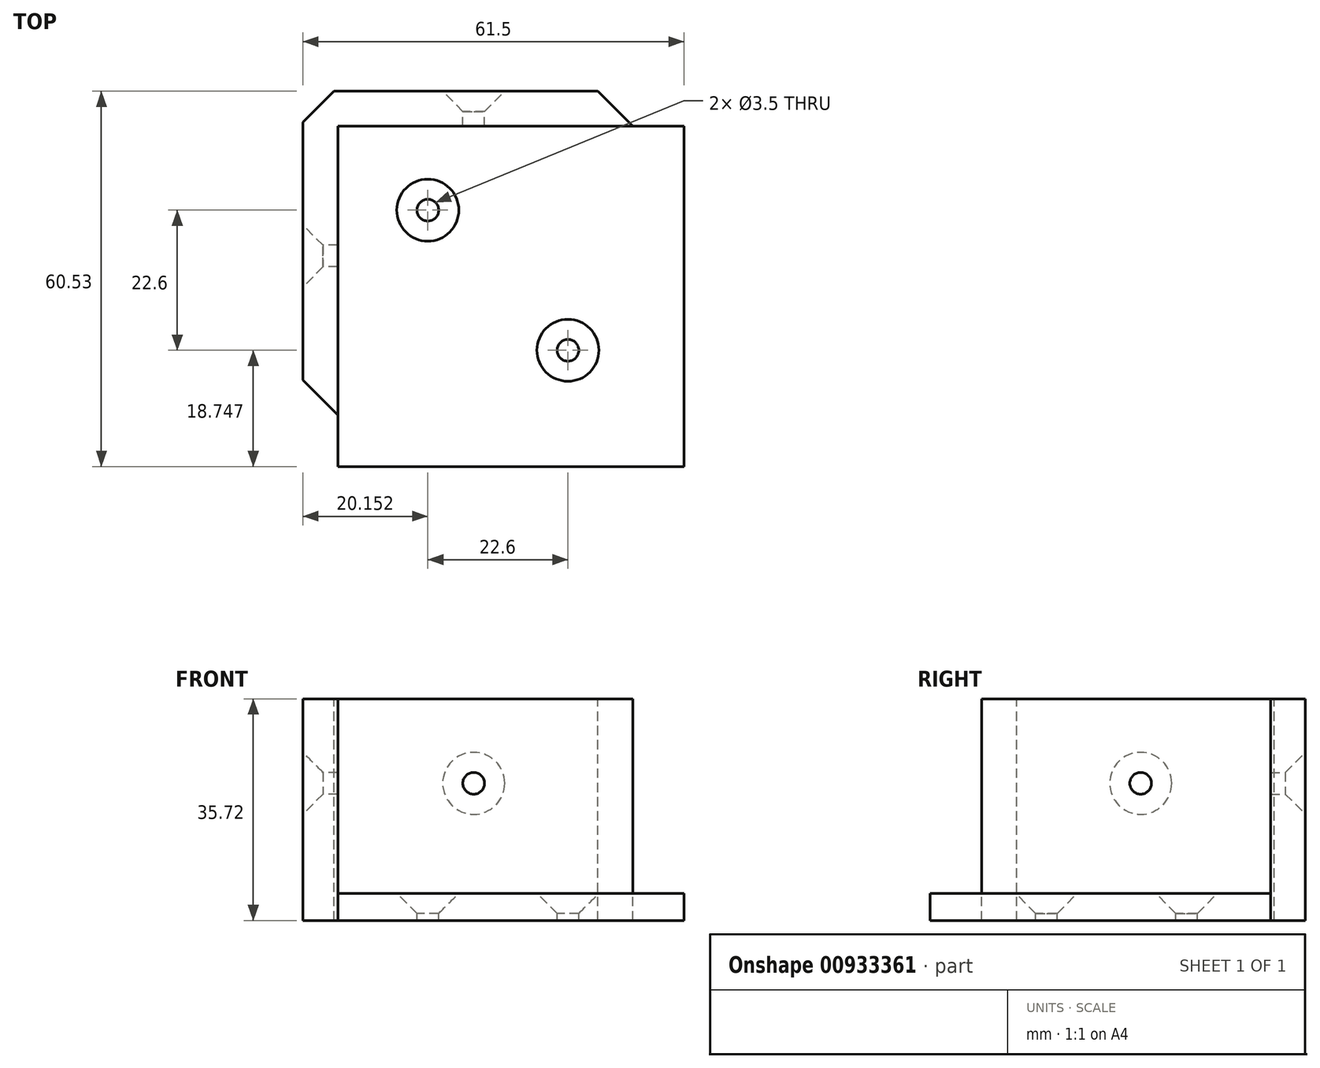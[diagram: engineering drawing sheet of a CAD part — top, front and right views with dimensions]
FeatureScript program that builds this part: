
annotation { "Feature Type Name" : "Feature", "Feature Type Description" : "" }
export const myFeature = defineFeature(function(context is Context, id is Id, definition is map)
    precondition{}
    {
        {
            var Q0;
            Q0=qCreatedBy(makeId("Top.planeOp"),FACE);
            var sketch = newSketch(context, id + "F0", { "sketchPlane" : qUnion([Q0])});
            skLineSegment(sketch, "E0.bottom", {"start": v(-41.05, 39.15) * mm, "end": v(20.45, 39.15) * mm});
            skLineSegment(sketch, "E0.top", {"start": v(-41.05, -21.38) * mm, "end": v(20.45, -21.38) * mm});
            skLineSegment(sketch, "E0.left", {"start": v(-41.05, 39.15) * mm, "end": v(-41.05, -21.38) * mm});
            skLineSegment(sketch, "E0.right", {"start": v(20.45, 39.15) * mm, "end": v(20.45, -21.38) * mm});
            skSolve(sketch);
        }
        {
            var Q0;
            Q0=makeQuery(id+"F0.imprint","IMPRINT",FACE,{"disambiguationData":[TD([[makeQuery(id+"F0.imprint","IMPRINT",EDGE,{"derivedFrom":sQuery(id+"F0.wireOp",EDGE,"E0.bottom")}),-1.0]])]});
            extrude(context, id + "F1", {"entities" : qUnion([Q0]), "depth" : 4.38 * mm, "offsetDistance" : 25 * mm});
        }
        {
            var Q0;
            Q0=makeQuery(id+"F1.opExtrude","CAP_FACE",FACE,{"disambiguationData":[OSD([sQuery(id+"F0.wireOp",EDGE,"E0.bottom"),sQuery(id+"F0.wireOp",EDGE,"E0.top"),sQuery(id+"F0.wireOp",EDGE,"E0.left"),sQuery(id+"F0.wireOp",EDGE,"E0.right")])],"isStart":false});
            var sketch = newSketch(context, id + "F2", { "sketchPlane" : qUnion([Q0])});
            skLineSegment(sketch, "E1.bottom", {"start": v(-41.05, -21.38) * mm, "end": v(-35.4, -21.38) * mm});
            skLineSegment(sketch, "E1.top", {"start": v(-41.05, 39.15) * mm, "end": v(-35.4, 39.15) * mm});
            skLineSegment(sketch, "E1.left", {"start": v(-41.05, -21.38) * mm, "end": v(-41.05, 39.15) * mm});
            skLineSegment(sketch, "E1.right", {"start": v(-35.4, -21.38) * mm, "end": v(-35.4, 33.5) * mm});
            skLineSegment(sketch, "E2.bottom", {"start": v(20.45, 39.15) * mm, "end": v(-35.4, 39.15) * mm});
            skLineSegment(sketch, "E2.top", {"start": v(20.45, 33.5) * mm, "end": v(-35.4, 33.5) * mm});
            skLineSegment(sketch, "E2.left", {"start": v(20.45, 39.15) * mm, "end": v(20.45, 33.5) * mm});
            skSolve(sketch);
        }
        {
            var Q0;
            Q0=makeQuery(id+"F2.imprint","IMPRINT",FACE,{"disambiguationData":[TD([[makeQuery(id+"F2.imprint","IMPRINT",EDGE,{"derivedFrom":sQuery(id+"F2.wireOp",EDGE,"E1.bottom")}),1.0]])]});
            extrude(context, id + "F3", {"entities" : qUnion([Q0]), "operationType" : NewBodyOperationType.ADD, "depth" : 31.34 * mm, "offsetDistance" : 25 * mm});
        }
        {
            var Q0;
            Q0=makeQuery(id+"F3.opExtrude","CAP_FACE",FACE,{"disambiguationData":[OSD([sQuery(id+"F2.wireOp",EDGE,"E1.bottom"),sQuery(id+"F2.wireOp",EDGE,"E1.top"),sQuery(id+"F2.wireOp",EDGE,"E1.left"),sQuery(id+"F2.wireOp",EDGE,"E1.right"),sQuery(id+"F2.wireOp",EDGE,"E2.bottom"),sQuery(id+"F2.wireOp",EDGE,"E2.top"),sQuery(id+"F2.wireOp",EDGE,"E2.left")])],"isStart":false});
            var sketch = newSketch(context, id + "F4", { "sketchPlane" : qUnion([Q0])});
            skLineSegment(sketch, "E3.bottom", {"start": v(-41.05, -21.38) * mm, "end": v(-35.4, -21.38) * mm});
            skLineSegment(sketch, "E3.top", {"start": v(-41.05, -13.08) * mm, "end": v(-35.4, -13.08) * mm});
            skLineSegment(sketch, "E3.left", {"start": v(-41.05, -21.38) * mm, "end": v(-41.05, -13.08) * mm});
            skLineSegment(sketch, "E3.right", {"start": v(-35.4, -21.38) * mm, "end": v(-35.4, -13.08) * mm});
            skLineSegment(sketch, "E4.bottom", {"start": v(20.45, 39.15) * mm, "end": v(12.15, 39.15) * mm});
            skLineSegment(sketch, "E4.top", {"start": v(20.45, 33.5) * mm, "end": v(12.15, 33.5) * mm});
            skLineSegment(sketch, "E4.left", {"start": v(20.45, 39.15) * mm, "end": v(20.45, 33.5) * mm});
            skLineSegment(sketch, "E4.right", {"start": v(12.15, 39.15) * mm, "end": v(12.15, 33.5) * mm});
            skSolve(sketch);
        }
        {
            var Q0;
            Q0=makeQuery(id+"F4.imprint","IMPRINT",FACE,{"disambiguationData":[TD([[makeQuery(id+"F4.imprint","IMPRINT",EDGE,{"derivedFrom":sQuery(id+"F4.wireOp",EDGE,"E3.bottom")}),1.0]])]});
            var Q1;
            Q1=makeQuery(id+"F4.imprint","IMPRINT",FACE,{"disambiguationData":[TD([[makeQuery(id+"F4.imprint","IMPRINT",EDGE,{"derivedFrom":sQuery(id+"F4.wireOp",EDGE,"E4.bottom")}),-1.0]])]});
            var Q2;
            Q2=makeQuery(id+"F1.opExtrude","CAP_FACE",FACE,{"disambiguationData":[OSD([sQuery(id+"F0.wireOp",EDGE,"E0.bottom"),sQuery(id+"F0.wireOp",EDGE,"E0.top"),sQuery(id+"F0.wireOp",EDGE,"E0.left"),sQuery(id+"F0.wireOp",EDGE,"E0.right")])],"isStart":true});
            extrude(context, id + "F5", {"entities" : qUnion([Q0, Q1]), "operationType" : NewBodyOperationType.REMOVE, "endBound" : BoundingType.UP_TO_SURFACE, "oppositeDirection" : true, "depth" : 25 * mm, "endBoundEntityFace" : qUnion([Q2]), "offsetDistance" : 25 * mm});
        }
        {
            var Q0;
            Q0=makeQuery(id+"F3.opExtrude","CAP_FACE",FACE,{"disambiguationData":[OSD([sQuery(id+"F2.wireOp",EDGE,"E1.bottom"),sQuery(id+"F2.wireOp",EDGE,"E1.top"),sQuery(id+"F2.wireOp",EDGE,"E1.left"),sQuery(id+"F2.wireOp",EDGE,"E1.right"),sQuery(id+"F2.wireOp",EDGE,"E2.bottom"),sQuery(id+"F2.wireOp",EDGE,"E2.top"),sQuery(id+"F2.wireOp",EDGE,"E2.left")])],"isStart":false});
            var sketch = newSketch(context, id + "F6", { "sketchPlane" : qUnion([Q0])});
            skLineSegment(sketch, "E5", {"start": v(-35.4, -13.08) * mm, "end": v(-41.05, -7.43) * mm});
            skLineSegment(sketch, "E6.0", {"start": v(-41.05, -13.08) * mm, "end": v(-35.4, -13.08) * mm});
            skLineSegment(sketch, "E7.0", {"start": v(-41.05, -7.43) * mm, "end": v(-41.05, -13.08) * mm});
            skPoint(sketch, "E8.orphan", {"position": v(-41.05, 39.15) * mm});
            skLineSegment(sketch, "E9", {"start": v(12.15, 33.5) * mm, "end": v(6.5, 39.15) * mm});
            skLineSegment(sketch, "E10.0", {"start": v(12.15, 39.15) * mm, "end": v(12.15, 33.5) * mm});
            skLineSegment(sketch, "E11.0", {"start": v(6.5, 39.15) * mm, "end": v(12.15, 39.15) * mm});
            skSolve(sketch);
        }
        {
            var Q0;
            Q0=makeQuery(id+"F6.imprint","IMPRINT",FACE,{"disambiguationData":[TD([[makeQuery(id+"F6.imprint","IMPRINT",EDGE,{"derivedFrom":sQuery(id+"F6.wireOp",EDGE,"E5")}),1.0]])]});
            var Q1;
            Q1=makeQuery(id+"F6.imprint","IMPRINT",FACE,{"disambiguationData":[TD([[makeQuery(id+"F6.imprint","IMPRINT",EDGE,{"derivedFrom":sQuery(id+"F6.wireOp",EDGE,"E9")}),-1.0]])]});
            var Q2;
            Q2=makeQuery(id+"F1.opExtrude","CAP_FACE",FACE,{"disambiguationData":[OSD([sQuery(id+"F0.wireOp",EDGE,"E0.bottom"),sQuery(id+"F0.wireOp",EDGE,"E0.top"),sQuery(id+"F0.wireOp",EDGE,"E0.left"),sQuery(id+"F0.wireOp",EDGE,"E0.right")])],"isStart":true});
            extrude(context, id + "F7", {"entities" : qUnion([Q0, Q1]), "operationType" : NewBodyOperationType.REMOVE, "endBound" : BoundingType.UP_TO_SURFACE, "oppositeDirection" : true, "depth" : 25 * mm, "endBoundEntityFace" : qUnion([Q2]), "offsetDistance" : 25 * mm});
        }
        {
            var Q0;
            Q0=makeQuery(id+"F3.opExtrude","CAP_FACE",FACE,{"disambiguationData":[OSD([sQuery(id+"F2.wireOp",EDGE,"E1.bottom"),sQuery(id+"F2.wireOp",EDGE,"E1.top"),sQuery(id+"F2.wireOp",EDGE,"E1.left"),sQuery(id+"F2.wireOp",EDGE,"E1.right"),sQuery(id+"F2.wireOp",EDGE,"E2.bottom"),sQuery(id+"F2.wireOp",EDGE,"E2.top"),sQuery(id+"F2.wireOp",EDGE,"E2.left")])],"isStart":false});
            var sketch = newSketch(context, id + "F8", { "sketchPlane" : qUnion([Q0])});
            skLineSegment(sketch, "E12", {"start": v(-36.03, 39.15) * mm, "end": v(-41.05, 34.13) * mm});
            skLineSegment(sketch, "E13.0", {"start": v(-41.05, 39.15) * mm, "end": v(-36.03, 39.15) * mm});
            skLineSegment(sketch, "E14.0", {"start": v(-41.05, 39.15) * mm, "end": v(-41.05, 34.13) * mm});
            skPoint(sketch, "E15.orphan", {"position": v(6.5, 39.15) * mm});
            skPoint(sketch, "E16.orphan", {"position": v(-41.05, -7.43) * mm});
            skSolve(sketch);
        }
        {
            var Q0;
            Q0=makeQuery(id+"F8.imprint","IMPRINT",FACE,{"disambiguationData":[TD([[makeQuery(id+"F8.imprint","IMPRINT",EDGE,{"derivedFrom":sQuery(id+"F8.wireOp",EDGE,"E12")}),-1.0]])]});
            var Q1;
            Q1=makeQuery(id+"F1.opExtrude","CAP_FACE",FACE,{"disambiguationData":[OSD([sQuery(id+"F0.wireOp",EDGE,"E0.bottom"),sQuery(id+"F0.wireOp",EDGE,"E0.top"),sQuery(id+"F0.wireOp",EDGE,"E0.left"),sQuery(id+"F0.wireOp",EDGE,"E0.right")])],"isStart":true});
            extrude(context, id + "F9", {"entities" : qUnion([Q0]), "operationType" : NewBodyOperationType.REMOVE, "endBound" : BoundingType.UP_TO_SURFACE, "oppositeDirection" : true, "depth" : 25 * mm, "endBoundEntityFace" : qUnion([Q1]), "offsetDistance" : 25 * mm});
        }
        {
            var Q0;
            Q0=makeQuery(id+"F1.opExtrude","CAP_FACE",FACE,{"disambiguationData":[OSD([sQuery(id+"F0.wireOp",EDGE,"E0.bottom"),sQuery(id+"F0.wireOp",EDGE,"E0.top"),sQuery(id+"F0.wireOp",EDGE,"E0.left"),sQuery(id+"F0.wireOp",EDGE,"E0.right")])],"isStart":false});
            var sketch = newSketch(context, id + "F10", { "sketchPlane" : qUnion([Q0])});
            skCircle(sketch, "E17", {"center": v(1.7, -2.63) * mm, "radius": 1.75 * mm});
            skSolve(sketch);
        }
        {
            var Q0;
            Q0=sQuery(id+"F10.wireOp",VERTEX,"E17.center");
            var Q1;
            Q1=makeQuery(id+"F1.opExtrude","SWEPT_BODY",BODY,{"disambiguationData":[OSD([sQuery(id+"F0.wireOp",EDGE,"E0.bottom"),sQuery(id+"F0.wireOp",EDGE,"E0.top"),sQuery(id+"F0.wireOp",EDGE,"E0.left"),sQuery(id+"F0.wireOp",EDGE,"E0.right")])]});
            hole(context, id + "F11", {"style" : HoleStyle.C_SINK, "endStyle" : HoleEndStyle.THROUGH, "holeDiameter" : 3.5 * mm, "cSinkDiameter" : 10 * mm, "cSinkAngle" : 90 * degree, "majorDiameter" : 5 * mm, "isTappedThrough" : true, "tappedDepth" : 12 * mm, "tapClearance" : 3, "startFromSketch" : true, "locations" : qUnion([Q0]), "scope" : qUnion([Q1])});
        }
        {
            var Q0;
            Q0=makeQuery(id+"F1.opExtrude","CAP_FACE",FACE,{"disambiguationData":[OSD([sQuery(id+"F0.wireOp",EDGE,"E0.bottom"),sQuery(id+"F0.wireOp",EDGE,"E0.top"),sQuery(id+"F0.wireOp",EDGE,"E0.left"),sQuery(id+"F0.wireOp",EDGE,"E0.right")])],"isStart":false});
            var sketch = newSketch(context, id + "F12", { "sketchPlane" : qUnion([Q0])});
            skPoint(sketch, "E18", {"position": v(-20.9, 19.97) * mm});
            skSolve(sketch);
        }
        {
            var Q0;
            Q0=sQuery(id+"F12.wireOp",VERTEX,"E18");
            var Q1;
            Q1=makeQuery(id+"F1.opExtrude","SWEPT_BODY",BODY,{"disambiguationData":[OSD([sQuery(id+"F0.wireOp",EDGE,"E0.bottom"),sQuery(id+"F0.wireOp",EDGE,"E0.top"),sQuery(id+"F0.wireOp",EDGE,"E0.left"),sQuery(id+"F0.wireOp",EDGE,"E0.right")])]});
            hole(context, id + "F13", {"style" : HoleStyle.C_SINK, "endStyle" : HoleEndStyle.THROUGH, "holeDiameter" : 3.5 * mm, "cSinkDiameter" : 10 * mm, "cSinkAngle" : 90 * degree, "majorDiameter" : 5 * mm, "isTappedThrough" : true, "tappedDepth" : 12 * mm, "tapClearance" : 3, "locations" : qUnion([Q0]), "scope" : qUnion([Q1])});
        }
        {
            var Q0;
            Q0=makeQuery(id+"F3.boolean.opBoolean","MERGE",FACE,{"derivedFrom":[makeQuery(id+"F1.opExtrude","SWEPT_FACE",FACE,{"disambiguationData":[OSD([sQuery(id+"F0.wireOp",EDGE,"E0.bottom")])]}),makeQuery(id+"F3.opExtrude","SWEPT_FACE",FACE,{"disambiguationData":[OSD([sQuery(id+"F2.wireOp",EDGE,"E1.top"),sQuery(id+"F2.wireOp",EDGE,"E2.bottom")])]})]});
            var sketch = newSketch(context, id + "F14", { "sketchPlane" : qUnion([Q0])});
            skPoint(sketch, "E19", {"position": v(13.5, 22.12) * mm});
            skSolve(sketch);
        }
        {
            var Q0;
            Q0=sQuery(id+"F14.wireOp",VERTEX,"E19");
            var Q1;
            Q1=makeQuery(id+"F1.opExtrude","SWEPT_BODY",BODY,{"disambiguationData":[OSD([sQuery(id+"F0.wireOp",EDGE,"E0.bottom"),sQuery(id+"F0.wireOp",EDGE,"E0.top"),sQuery(id+"F0.wireOp",EDGE,"E0.left"),sQuery(id+"F0.wireOp",EDGE,"E0.right")])]});
            hole(context, id + "F15", {"style" : HoleStyle.C_SINK, "endStyle" : HoleEndStyle.THROUGH, "holeDiameter" : 3.5 * mm, "cSinkDiameter" : 10 * mm, "cSinkAngle" : 90 * degree, "majorDiameter" : 5 * mm, "isTappedThrough" : true, "tappedDepth" : 12 * mm, "tapClearance" : 3, "locations" : qUnion([Q0]), "scope" : qUnion([Q1])});
        }
        {
            var Q0;
            Q0=makeQuery(id+"F3.boolean.opBoolean","MERGE",FACE,{"derivedFrom":[makeQuery(id+"F1.opExtrude","SWEPT_FACE",FACE,{"disambiguationData":[OSD([sQuery(id+"F0.wireOp",EDGE,"E0.left")])]}),makeQuery(id+"F3.opExtrude","SWEPT_FACE",FACE,{"disambiguationData":[OSD([sQuery(id+"F2.wireOp",EDGE,"E1.left")])]})]});
            var sketch = newSketch(context, id + "F16", { "sketchPlane" : qUnion([Q0])});
            skPoint(sketch, "E20", {"position": v(-12.57, 22.12) * mm});
            skSolve(sketch);
        }
        {
            var Q0;
            Q0=sQuery(id+"F16.wireOp",VERTEX,"E20");
            var Q1;
            Q1=makeQuery(id+"F1.opExtrude","SWEPT_BODY",BODY,{"disambiguationData":[OSD([sQuery(id+"F0.wireOp",EDGE,"E0.bottom"),sQuery(id+"F0.wireOp",EDGE,"E0.top"),sQuery(id+"F0.wireOp",EDGE,"E0.left"),sQuery(id+"F0.wireOp",EDGE,"E0.right")])]});
            hole(context, id + "F17", {"style" : HoleStyle.C_SINK, "endStyle" : HoleEndStyle.THROUGH, "holeDiameter" : 3.5 * mm, "cSinkDiameter" : 10 * mm, "cSinkAngle" : 90 * degree, "majorDiameter" : 5 * mm, "isTappedThrough" : true, "tappedDepth" : 12 * mm, "tapClearance" : 3, "locations" : qUnion([Q0]), "scope" : qUnion([Q1])});
        }
    });
